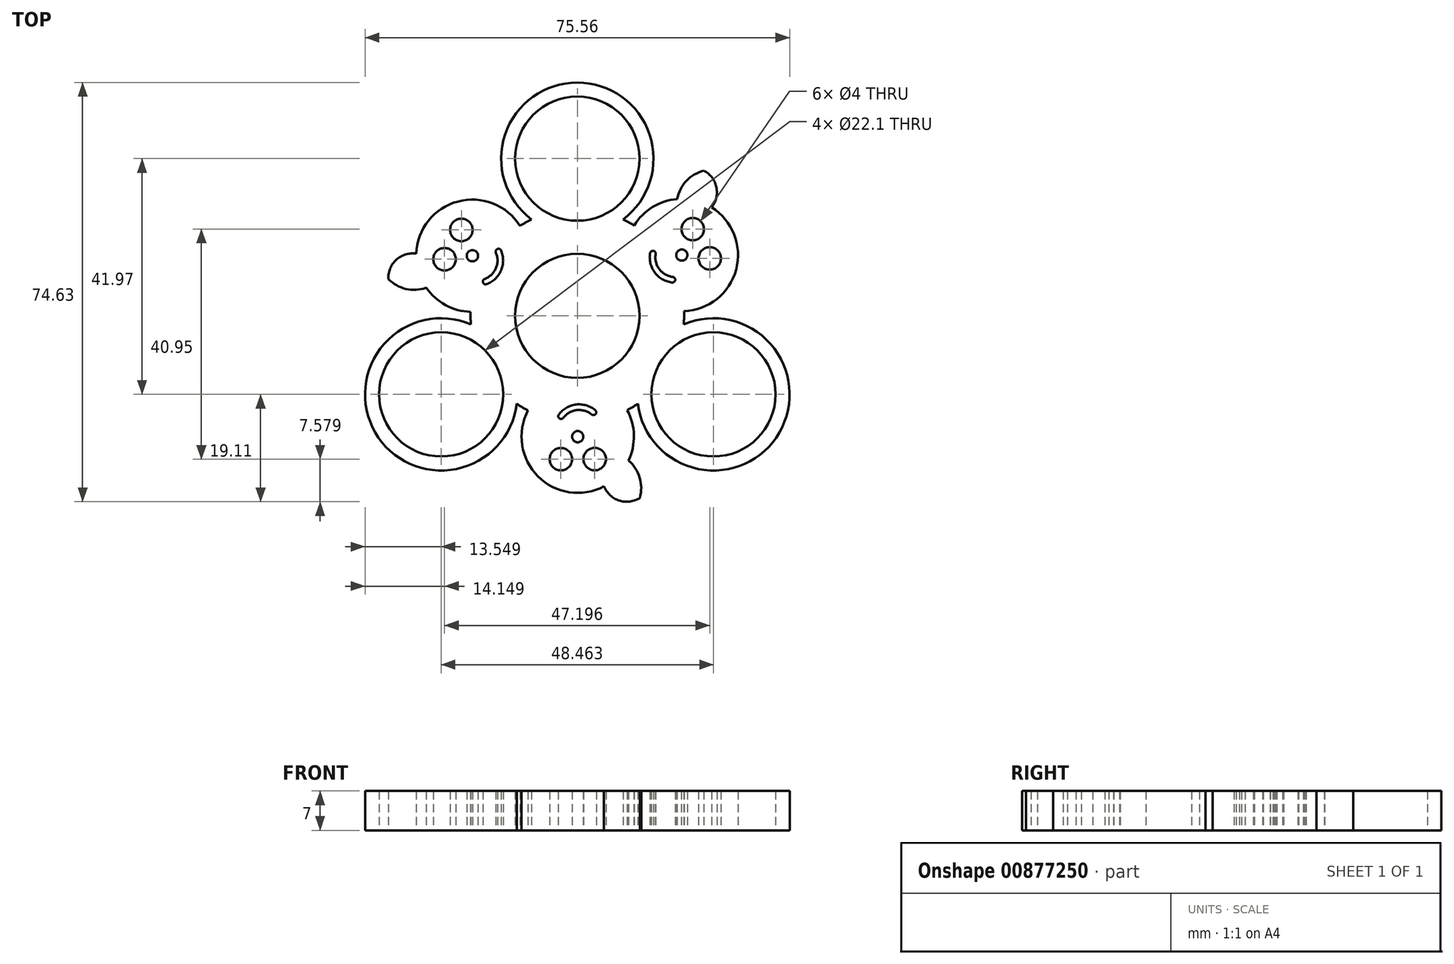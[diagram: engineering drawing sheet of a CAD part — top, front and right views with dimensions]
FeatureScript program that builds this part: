
annotation { "Feature Type Name" : "Feature", "Feature Type Description" : "" }
export const myFeature = defineFeature(function(context is Context, id is Id, definition is map)
    precondition{}
    {
        {
            var Q0;
            Q0=qCreatedBy(makeId("Top.planeOp"),FACE);
            var sketch = newSketch(context, id + "F0", { "sketchPlane" : qUnion([Q0])});
            skCircle(sketch, "E0", {"center": v(0, 0) * mm, "radius": 11.05 * mm});
            skCircle(sketch, "E1", {"center": v(0, 0) * mm, "radius": 13.55 * mm});
            skCircle(sketch, "E2", {"center": v(0, 27.98) * mm, "radius": 11.05 * mm});
            skCircle(sketch, "E3", {"center": v(0, 27.98) * mm, "radius": 13.55 * mm});
            skCircle(sketch, "E4.1.0", {"center": v(-24.23, -13.99) * mm, "radius": 11.05 * mm});
            skCircle(sketch, "E4.1.1", {"center": v(-24.23, -13.99) * mm, "radius": 13.55 * mm});
            skCircle(sketch, "E4.2.0", {"center": v(24.23, -13.99) * mm, "radius": 11.05 * mm});
            skCircle(sketch, "E4.2.1", {"center": v(24.23, -13.99) * mm, "radius": 13.55 * mm});
            skArc(sketch, "E5", {"start": v(-8.67, 10.4) * mm, "mid": v(-27.35, 15.67) * mm, "end": v(-13.37, 2.22) * mm});
            skArc(sketch, "E6.1.0", {"start": v(-4.68, -12.72) * mm, "mid": v(0.1, -31.52) * mm, "end": v(4.76, -12.69) * mm});
            skArc(sketch, "E6.2.0", {"start": v(13.35, 2.3) * mm, "mid": v(27.24, 15.85) * mm, "end": v(8.6, 10.47) * mm});
            skArc(sketch, "E7", {"start": v(-33.64, 6.57) * mm, "mid": v(-30.5, 4.8) * mm, "end": v(-26.88, 5) * mm});
            skArc(sketch, "E8", {"start": v(-28.66, 11.06) * mm, "mid": v(-32.2, 9.99) * mm, "end": v(-33.64, 6.57) * mm});
            skLineSegment(sketch, "E9", {"start": v(0, 0) * mm, "end": v(-18.67, 10.7) * mm, "construction": true});
            skArc(sketch, "E10.MirrorCS", {"start": v(-24.04, 19.14) * mm, "mid": v(-24.9, 22.74) * mm, "end": v(-22.68, 25.7) * mm});
            skArc(sketch, "E11.MirrorCS", {"start": v(-22.68, 25.7) * mm, "mid": v(-19.56, 23.88) * mm, "end": v(-17.9, 20.67) * mm});
            skArc(sketch, "E12.1.0", {"start": v(-10.92, -32.5) * mm, "mid": v(-10.9, -28.88) * mm, "end": v(-8.95, -25.84) * mm});
            skArc(sketch, "E12.1.1", {"start": v(-4.56, -30.38) * mm, "mid": v(-7.24, -32.93) * mm, "end": v(-10.92, -32.5) * mm});
            skArc(sketch, "E12.1.2", {"start": v(4.75, -30.35) * mm, "mid": v(7.46, -32.89) * mm, "end": v(11.13, -32.42) * mm});
            skArc(sketch, "E12.1.3", {"start": v(11.13, -32.42) * mm, "mid": v(11.1, -28.8) * mm, "end": v(9.12, -25.78) * mm});
            skArc(sketch, "E12.2.0", {"start": v(33.6, 6.79) * mm, "mid": v(30.46, 5) * mm, "end": v(26.85, 5.17) * mm});
            skArc(sketch, "E12.2.1", {"start": v(28.6, 11.25) * mm, "mid": v(32.14, 10.2) * mm, "end": v(33.6, 6.79) * mm});
            skArc(sketch, "E12.2.2", {"start": v(23.91, 19.3) * mm, "mid": v(24.75, 22.9) * mm, "end": v(22.51, 25.85) * mm});
            skArc(sketch, "E12.2.3", {"start": v(22.51, 25.85) * mm, "mid": v(19.4, 24) * mm, "end": v(17.76, 20.78) * mm});
            skArc(sketch, "E13", {"start": v(-18.99, 0.7) * mm, "mid": v(-19, -0.4) * mm, "end": v(-18.94, -1.52) * mm});
            skArc(sketch, "E14.trimOffspring", {"start": v(10.1, 16.1) * mm, "mid": v(9.15, 16.65) * mm, "end": v(8.16, 17.16) * mm});
            skArc(sketch, "E15.trimOffspring", {"start": v(8.88, -16.8) * mm, "mid": v(9.85, -16.25) * mm, "end": v(10.78, -15.64) * mm});
            skArc(sketch, "E16.trimOffspring", {"start": v(18.94, -1.52) * mm, "mid": v(19, -0.35) * mm, "end": v(18.98, 0.83) * mm});
            skArc(sketch, "E17.trimOffspring", {"start": v(-8.16, 17.16) * mm, "mid": v(-9.2, 16.62) * mm, "end": v(-10.2, 16.03) * mm});
            skArc(sketch, "E18.trimOffspring", {"start": v(-10.78, -15.64) * mm, "mid": v(-9.8, -16.28) * mm, "end": v(-8.77, -16.85) * mm});
            skLineSegment(sketch, "E19", {"start": v(-18.67, 10.7) * mm, "end": v(-20.64, 15.3) * mm, "construction": true});
            skLineSegment(sketch, "E20", {"start": v(-18.67, 10.7) * mm, "end": v(-23.63, 10.07) * mm, "construction": true});
            skCircle(sketch, "E21", {"center": v(-20.64, 15.3) * mm, "radius": 2 * mm});
            skCircle(sketch, "E22", {"center": v(-23.63, 10.07) * mm, "radius": 2 * mm});
            skArc(sketch, "E23", {"start": v(-16.14, 5.64) * mm, "mid": v(-13.57, 8.08) * mm, "end": v(-13.57, 11.63) * mm});
            skArc(sketch, "E24.0", {"start": v(-16.49, 6.57) * mm, "mid": v(-14.49, 8.48) * mm, "end": v(-14.49, 11.24) * mm});
            skArc(sketch, "E25", {"start": v(-16.49, 6.57) * mm, "mid": v(-16.78, 5.93) * mm, "end": v(-16.14, 5.64) * mm});
            skArc(sketch, "E26", {"start": v(-13.57, 11.63) * mm, "mid": v(-14.22, 11.9) * mm, "end": v(-14.49, 11.24) * mm});
            skCircle(sketch, "E27.1.0", {"center": v(-2.93, -25.52) * mm, "radius": 2 * mm});
            skCircle(sketch, "E27.1.1", {"center": v(3.1, -25.5) * mm, "radius": 2 * mm});
            skArc(sketch, "E27.1.2", {"start": v(2.55, -17.56) * mm, "mid": v(-0.1, -16.79) * mm, "end": v(-2.49, -18.17) * mm});
            skArc(sketch, "E27.1.3", {"start": v(3.19, -16.8) * mm, "mid": v(-0.22, -15.8) * mm, "end": v(-3.29, -17.57) * mm});
            skArc(sketch, "E27.1.4", {"start": v(2.55, -17.56) * mm, "mid": v(3.25, -17.5) * mm, "end": v(3.19, -16.8) * mm});
            skArc(sketch, "E27.1.5", {"start": v(-3.29, -17.57) * mm, "mid": v(-3.19, -18.27) * mm, "end": v(-2.49, -18.17) * mm});
            skCircle(sketch, "E27.2.0", {"center": v(23.57, 10.23) * mm, "radius": 2 * mm});
            skCircle(sketch, "E27.2.1", {"center": v(20.54, 15.43) * mm, "radius": 2 * mm});
            skArc(sketch, "E27.2.2", {"start": v(13.94, 11) * mm, "mid": v(14.59, 8.3) * mm, "end": v(16.98, 6.93) * mm});
            skArc(sketch, "E27.2.3", {"start": v(12.95, 11.16) * mm, "mid": v(13.79, 7.7) * mm, "end": v(16.86, 5.94) * mm});
            skArc(sketch, "E27.2.4", {"start": v(13.94, 11) * mm, "mid": v(13.53, 11.57) * mm, "end": v(12.95, 11.16) * mm});
            skArc(sketch, "E27.2.5", {"start": v(16.86, 5.94) * mm, "mid": v(17.41, 6.37) * mm, "end": v(16.98, 6.93) * mm});
            skCircle(sketch, "E28", {"center": v(-18.67, 10.7) * mm, "radius": 1 * mm});
            skCircle(sketch, "E29.1.0", {"center": v(0.07, -21.52) * mm, "radius": 1 * mm});
            skCircle(sketch, "E29.2.0", {"center": v(18.6, 10.82) * mm, "radius": 1 * mm});
            skSolve(sketch);
        }
        {
            var Q0;
            Q0=makeQuery(id+"F0.imprint","IMPRINT",FACE,{"disambiguationData":[TD([[makeQuery(id+"F0.imprint","IMPRINT",EDGE,{"derivedFrom":sQuery(id+"F0.wireOp",EDGE,"E2")}),-1.0]])]});
            var Q1;
            Q1=makeQuery(id+"F0.imprint","IMPRINT",FACE,{"disambiguationData":[TD([[makeQuery(id+"F0.imprint","IMPRINT",EDGE,{"derivedFrom":sQuery(id+"F0.wireOp",EDGE,"E4.2.0")}),-1.0]])]});
            var Q2;
            Q2=makeQuery(id+"F0.imprint","IMPRINT",FACE,{"disambiguationData":[TD([[makeQuery(id+"F0.imprint","IMPRINT",EDGE,{"derivedFrom":sQuery(id+"F0.wireOp",EDGE,"E4.1.0")}),-1.0]])]});
            var Q3;
            Q3=makeQuery(id+"F0.imprint","IMPRINT",FACE,{"disambiguationData":[TD([[makeQuery(id+"F0.imprint","IMPRINT",EDGE,{"derivedFrom":sQuery(id+"F0.wireOp",EDGE,"E0")}),-1.0]])]});
            var Q4;
            {var subQ6=sQuery(id+"F0.wireOp",EDGE,"E13");Q4=makeQuery(id+"F0.imprint","IMPRINT",FACE,{"disambiguationData":[TD([[makeQuery(id+"F0.imprint","IMPRINT",EDGE,{"derivedFrom":subQ6}),1.0]])]});}
            var Q5;
            {var subQ3=sQuery(id+"F0.wireOp",EDGE,"E14.trimOffspring");Q5=makeQuery(id+"F0.imprint","IMPRINT",FACE,{"disambiguationData":[TD([[makeQuery(id+"F0.imprint","IMPRINT",EDGE,{"derivedFrom":subQ3}),1.0]])]});}
            var Q6;
            {var subQ6=sQuery(id+"F0.wireOp",EDGE,"E15.trimOffspring");Q6=makeQuery(id+"F0.imprint","IMPRINT",FACE,{"disambiguationData":[TD([[makeQuery(id+"F0.imprint","IMPRINT",EDGE,{"derivedFrom":subQ6}),1.0]])]});}
            var Q7;
            Q7=makeQuery(id+"F0.imprint","IMPRINT",FACE,{"disambiguationData":[TD([[makeQuery(id+"F0.imprint","IMPRINT",EDGE,{"derivedFrom":sQuery(id+"F0.wireOp",EDGE,"E27.2.0")}),-1.0]])]});
            var Q8;
            {var subQ0=sQuery(id+"F0.wireOp",EDGE,"E12.2.0");Q8=makeQuery(id+"F0.imprint","IMPRINT",FACE,{"disambiguationData":[TD([[makeQuery(id+"F0.imprint","IMPRINT",EDGE,{"derivedFrom":subQ0}),-1.0]])]});}
            var Q9;
            {var subQ0=sQuery(id+"F0.wireOp",EDGE,"E12.2.2");Q9=makeQuery(id+"F0.imprint","IMPRINT",FACE,{"disambiguationData":[TD([[makeQuery(id+"F0.imprint","IMPRINT",EDGE,{"derivedFrom":subQ0}),1.0]])]});}
            var Q10;
            Q10=makeQuery(id+"F0.imprint","IMPRINT",FACE,{"disambiguationData":[TD([[makeQuery(id+"F0.imprint","IMPRINT",EDGE,{"derivedFrom":sQuery(id+"F0.wireOp",EDGE,"E21")}),-1.0]])]});
            var Q11;
            {var subQ0=sQuery(id+"F0.wireOp",EDGE,"E10.MirrorCS");Q11=makeQuery(id+"F0.imprint","IMPRINT",FACE,{"disambiguationData":[TD([[makeQuery(id+"F0.imprint","IMPRINT",EDGE,{"derivedFrom":subQ0}),-1.0]])]});}
            var Q12;
            {var subQ0=sQuery(id+"F0.wireOp",EDGE,"E7");Q12=makeQuery(id+"F0.imprint","IMPRINT",FACE,{"disambiguationData":[TD([[makeQuery(id+"F0.imprint","IMPRINT",EDGE,{"derivedFrom":subQ0}),1.0]])]});}
            var Q13;
            Q13=makeQuery(id+"F0.imprint","IMPRINT",FACE,{"disambiguationData":[TD([[makeQuery(id+"F0.imprint","IMPRINT",EDGE,{"derivedFrom":sQuery(id+"F0.wireOp",EDGE,"E27.1.0")}),-1.0]])]});
            var Q14;
            {var subQ0=sQuery(id+"F0.wireOp",EDGE,"E12.1.0");Q14=makeQuery(id+"F0.imprint","IMPRINT",FACE,{"disambiguationData":[TD([[makeQuery(id+"F0.imprint","IMPRINT",EDGE,{"derivedFrom":subQ0}),-1.0]])]});}
            var Q15;
            {var subQ0=sQuery(id+"F0.wireOp",EDGE,"E12.1.2");Q15=makeQuery(id+"F0.imprint","IMPRINT",FACE,{"disambiguationData":[TD([[makeQuery(id+"F0.imprint","IMPRINT",EDGE,{"derivedFrom":subQ0}),1.0]])]});}
            extrude(context, id + "F1", {"entities" : qUnion([Q0, Q1, Q2, Q3, Q4, Q5, Q6, Q7, Q8, Q9, Q10, Q11, Q12, Q13, Q14, Q15]), "depth" : 7 * mm, "offsetDistance" : 25 * mm});
        }
    });
